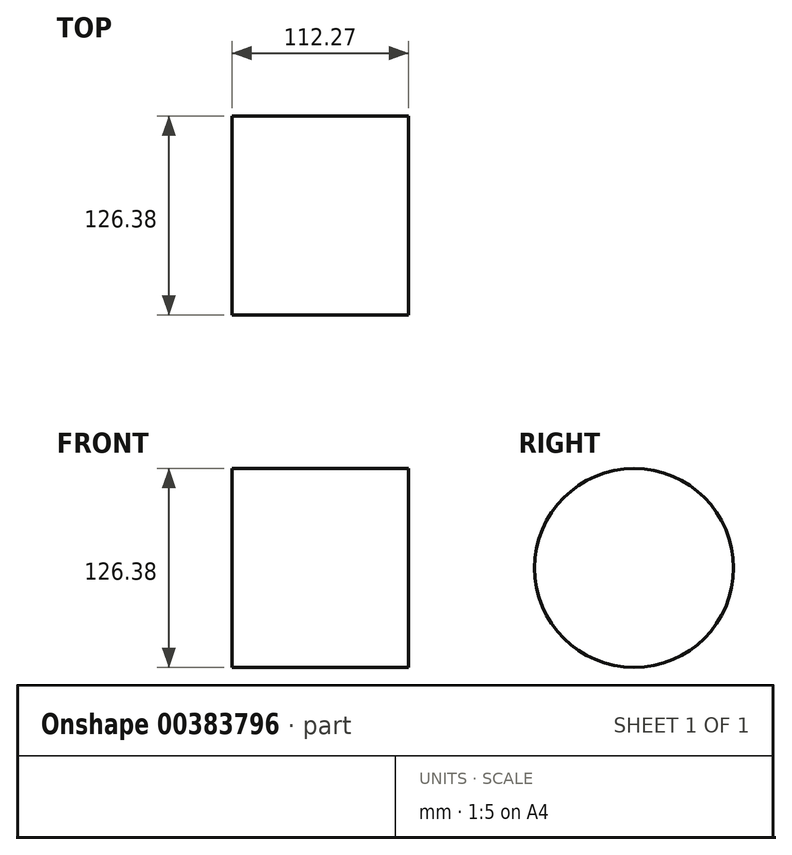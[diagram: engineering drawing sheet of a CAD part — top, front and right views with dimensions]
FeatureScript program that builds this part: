
annotation { "Feature Type Name" : "Feature", "Feature Type Description" : "" }
export const myFeature = defineFeature(function(context is Context, id is Id, definition is map)
    precondition{}
    {
        {
            var Q0;
            Q0=qCreatedBy(makeId("Right.planeOp"),FACE);
            var sketch = newSketch(context, id + "F0", { "sketchPlane" : qUnion([Q0])});
            skCircle(sketch, "E0", {"center": v(0, 0) * mm, "radius": 63.19 * mm});
            skSolve(sketch);
        }
        {
            var Q0;
            Q0=qCreatedBy(makeId("Front.planeOp"),FACE);
            var sketch = newSketch(context, id + "F1", { "sketchPlane" : qUnion([Q0])});
            skSolve(sketch);
        }
        {
            var Q0;
            Q0=makeQuery(id+"F0.imprint","IMPRINT",FACE,{"disambiguationData":[TD([[makeQuery(id+"F0.imprint","IMPRINT",EDGE,{"derivedFrom":sQuery(id+"F0.wireOp",EDGE,"E0")}),1.0]])]});
            extrude(context, id + "F2", {"entities" : qUnion([Q0]), "depth" : 25.4 * mm});
        }
        {
            var Q0;
            Q0 = qSketchRegion(id + "F0", true);
            var Q1;
            Q1 = qSketchRegion(id + "F1", true);
            extrude(context, id + "F3", {"entities" : qUnion([Q0, Q1]), "operationType" : NewBodyOperationType.ADD, "depth" : 112.27 * mm});
        }
    });
